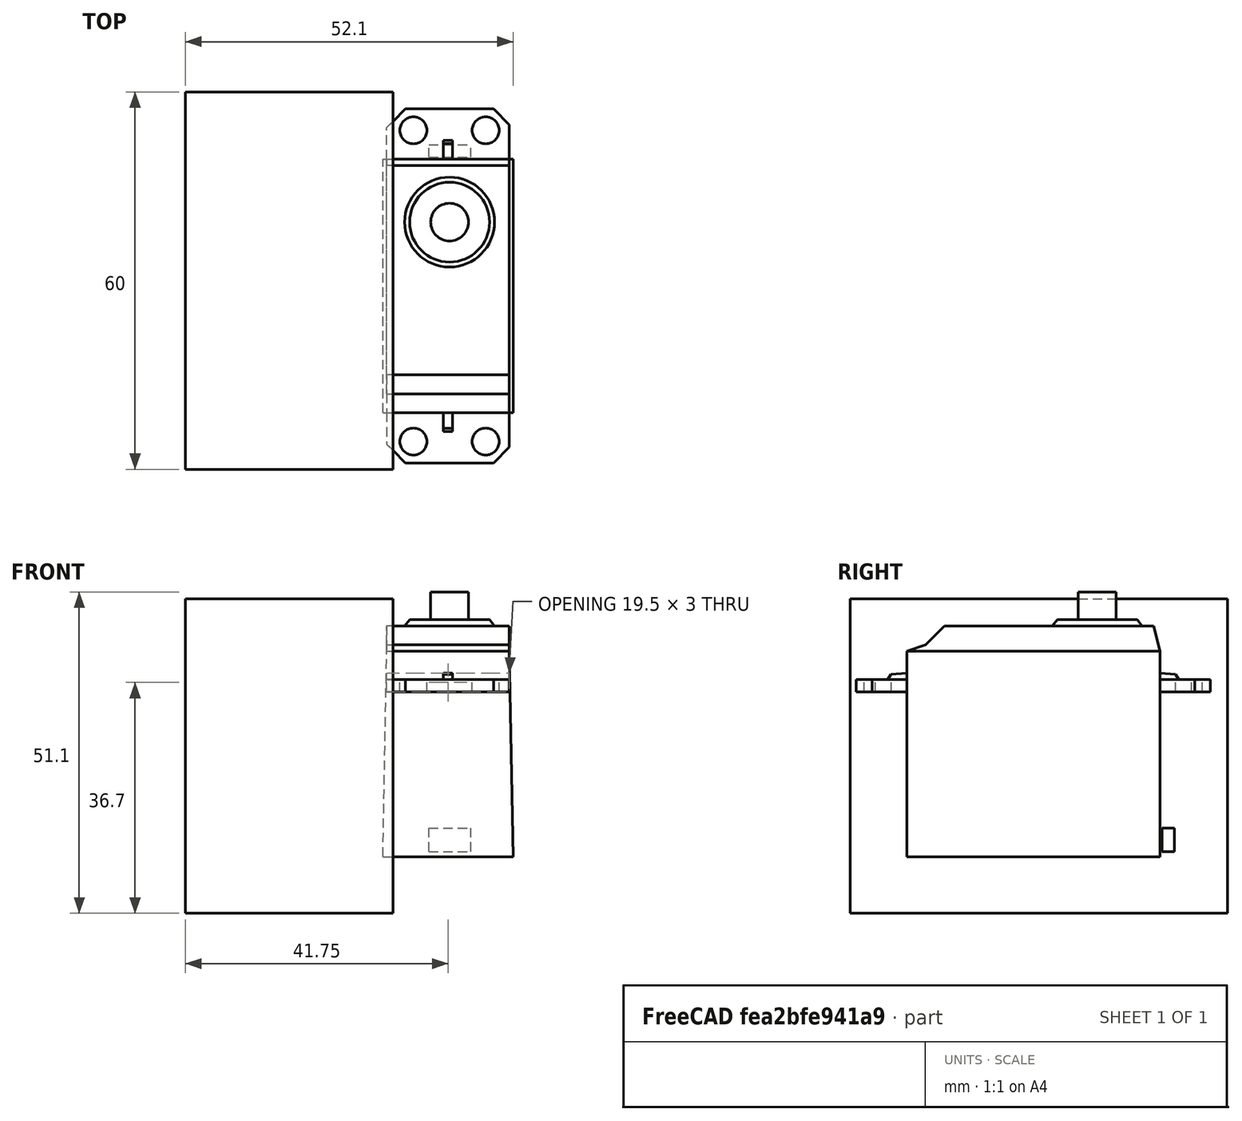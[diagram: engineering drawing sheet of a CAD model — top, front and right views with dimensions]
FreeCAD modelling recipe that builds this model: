
FCSTD DOCUMENT  (FreeCAD 0.16R4924 (Git))
Label: test
License: All rights reserved
LicenseURL: http://en.wikipedia.org/wiki/All_rights_reserved
objects: Part::Box×12, Part::Feature×8, Part::Mirroring×6, Part::Cylinder×5, Part::MultiFuse×5, Part::Cut×2, Part::Cone×1
note: 39 computed .brp shape members not serialized (recipe doc carries the construction recipe); baked Part::Feature solids carry a one-line shape summary decoded from their .brp

FEATURE [Part::Box] cube
  Height = 2
  Length = 19.5
  Width = 8
FEATURE [Part::Box] cube001
  Height = 4
  Length = 19.5
  Placement = pos=(0,5,-1) rot=(0,0,1;0.785398rad)
  Width = 8
FEATURE [Part::Box] cube002
  Height = 4
  Length = 19.5
  Placement = pos=(17,8,-1) rot=(0,0,-1;0.785398rad)
  Width = 8
FEATURE [Part::Cylinder] cylinder
  Angle = 360
  Height = 4
  Placement = pos=(4.25,4.6,-1) rot=(0,0,1;0rad)
  Radius = 2.15
FEATURE [Part::Cylinder] cylinder001
  Angle = 360
  Height = 4
  Placement = pos=(15.75,4.6,-1) rot=(0,0,1;0rad)
  Radius = 2.15
FEATURE [Part::MultiFuse] union
  Shapes = -> [cube001,cube002,cylinder,cylinder001]
FEATURE [Part::Cut] difference
  Base = -> cube
  Tool = -> union
FEATURE [Part::Box] cube003
  Height = 0.8
  Length = 1.5
  Placement = pos=(9,0,2) rot=(0,0,1;0rad)
  Width = 2.5
FEATURE [Part::Feature] polyhedron
  shape: bbox 1.5 x 2.5 x 0.2 mm, 5 faces (baked)
FEATURE [Part::Mirroring] mirr_polyhedron  label="mirrored polyhedron"
  Base = (0,0,0)
  Normal = (0,1,0)
  Placement = pos=(9,2.5,2.8) rot=(0,0,1;0rad)
  Source = -> polyhedron
FEATURE [Part::Feature] polyhedron001
  shape: bbox 1.5 x 0.5 x 0.8 mm, 5 faces (baked)
FEATURE [Part::Mirroring] mirr_polyhedron001  label="mirrored polyhedron001"
  Base = (0,0,0)
  Normal = (0,1,0)
  Placement = pos=(9,3,2) rot=(0,0,1;0rad)
  Source = -> polyhedron001
FEATURE [Part::MultiFuse] Group
  Placement = pos=(0,40.3,26.2) rot=(0,0,1;0rad)
  Shapes = -> [difference,cube003,mirr_polyhedron,mirr_polyhedron001]
FEATURE [Part::Box] cube004
  Height = 2
  Length = 19.5
  Width = 8
FEATURE [Part::Box] cube005
  Height = 4
  Length = 19.5
  Placement = pos=(0,5,-1) rot=(0,0,1;0.785398rad)
  Width = 8
FEATURE [Part::Box] cube006
  Height = 4
  Length = 19.5
  Placement = pos=(17,8,-1) rot=(0,0,-1;0.785398rad)
  Width = 8
FEATURE [Part::Cylinder] cylinder002
  Angle = 360
  Height = 4
  Placement = pos=(4.25,4.6,-1) rot=(0,0,1;0rad)
  Radius = 2.15
FEATURE [Part::Cylinder] cylinder003
  Angle = 360
  Height = 4
  Placement = pos=(15.75,4.6,-1) rot=(0,0,1;0rad)
  Radius = 2.15
FEATURE [Part::MultiFuse] union001
  Shapes = -> [cube005,cube006,cylinder002,cylinder003]
FEATURE [Part::Cut] difference001
  Base = -> cube004
  Tool = -> union001
FEATURE [Part::Box] cube007
  Height = 0.8
  Length = 1.5
  Placement = pos=(9,0,2) rot=(0,0,1;0rad)
  Width = 2.5
FEATURE [Part::Feature] polyhedron002
  shape: bbox 1.5 x 2.5 x 0.2 mm, 5 faces (baked)
FEATURE [Part::Mirroring] mirr_polyhedron002  label="mirrored polyhedron002"
  Base = (0,0,0)
  Normal = (0,1,0)
  Placement = pos=(9,2.5,2.8) rot=(0,0,1;0rad)
  Source = -> polyhedron002
FEATURE [Part::Feature] polyhedron003
  shape: bbox 1.5 x 0.5 x 0.8 mm, 5 faces (baked)
FEATURE [Part::Mirroring] mirr_polyhedron003  label="mirrored polyhedron003"
  Base = (0,0,0)
  Normal = (0,1,0)
  Placement = pos=(9,3,2) rot=(0,0,1;0rad)
  Source = -> polyhedron003
FEATURE [Part::MultiFuse] Group001
  Shapes = -> [difference001,cube007,mirr_polyhedron002,mirr_polyhedron003]
FEATURE [Part::Mirroring] mirr_Group001  label="mirrored Group001"
  Base = (0,0,0)
  Normal = (0,1,0)
  Placement = pos=(0,0,26.2) rot=(0,0,1;0rad)
  Source = -> Group001
FEATURE [Part::Feature] polyhedron004
  shape: bbox 20.7 x 40.3 x 32.7 mm, 6 faces (baked)
FEATURE [Part::Box] cube008
  Height = 1
  Length = 19.5
  Placement = pos=(0,3,32.7) rot=(0,0,1;0rad)
  Width = 36.4
FEATURE [Part::Box] cube009
  Height = 3
  Length = 19.5
  Placement = pos=(0,6,33.7) rot=(0,0,1;0rad)
  Width = 33.3
FEATURE [Part::Feature] polyhedron005
  shape: bbox 19.5 x 1 x 4 mm, 5 faces (baked)
FEATURE [Part::Mirroring] mirr_polyhedron005  label="mirrored polyhedron005"
  Base = (0,0,0)
  Normal = (0,1,0)
  Placement = pos=(0,40.3,32.7) rot=(0,0,1;0rad)
  Source = -> polyhedron005
FEATURE [Part::Feature] polyhedron006
  Placement = pos=(0,0,32.7) rot=(0,0,1;0rad)
  shape: bbox 19.5 x 3 x 1 mm, 5 faces (baked)
FEATURE [Part::Feature] polyhedron007
  Placement = pos=(0,3,33.7) rot=(0,0,1;0rad)
  shape: bbox 19.5 x 3 x 3 mm, 5 faces (baked)
FEATURE [Part::Cone] cylinder004
  Angle = 360
  Height = 1
  Placement = pos=(10,30.3,36.7) rot=(0,0,1;0rad)
  Radius1 = 7.15
  Radius2 = 6.35
FEATURE [Part::Box] cube010
  Height = 3.75
  Length = 6.7
  Placement = pos=(6.7,40.6,0.8) rot=(0,0,1;0rad)
  Width = 2
FEATURE [Part::Cylinder] cylinder005
  Angle = 360
  Height = 5.4
  Placement = pos=(10,30.3,36.7) rot=(0,0,1;0rad)
  Radius = 3
FEATURE [Part::MultiFuse] Group002
  Placement = pos=(14,9,9) rot=(0,0,1;0rad)
  Shapes = -> [Group,mirr_Group001,polyhedron004,cube008,cube009,mirr_polyhedron005,polyhedron006,polyhedron007,cylinder004,cube010,cylinder005]
FEATURE [Part::Box] Box  label="Cube"
  Height = 50
  Length = 33
  Placement = pos=(-18,0,0) rot=(0,0,1;0rad)
  Width = 60
